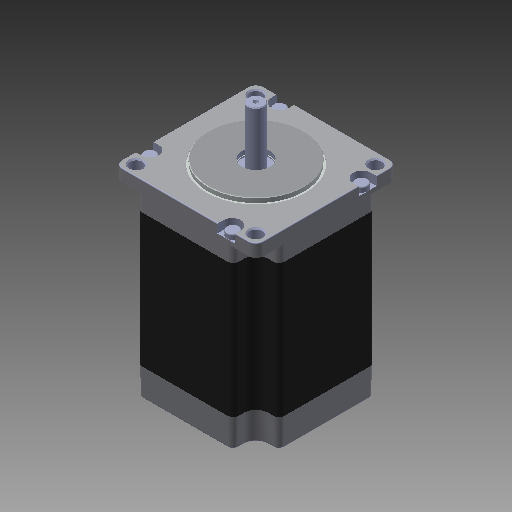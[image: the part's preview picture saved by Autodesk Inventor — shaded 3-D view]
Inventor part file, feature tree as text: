
AUTODESK INVENTOR PART (.ipt)
format: ipt  version: 2018 (Build 220112000, 112)  size: 415,744 bytes
history: native  units: in
note: dims shown in document units (in); Inventor stores cm internally (conversion verified against a paired STEP export)
features: other x3, imported_body x2, extrude x1, sketch x1
ambient origin geometry x8: Origin, YZ Plane, XZ Plane, XY Plane, X Axis, Y Axis, Z Axis, Center Point
bodies: Body1 (feature_tree), Body2 (feature_tree), Body3 (feature_tree), Body4 (feature_tree)
feature tree (7):
  other  "Фаска2"
  other  "stepper motor NEMA 23 57x761"
  extrude  "Extrusion1"  [1 undecoded]
  other  "Вырез-Вытянуть12"
  imported_body  "Base1"
  imported_body  "Base2"
  sketch  "Sketch1"  dims[d0=0.5906in d1=0.0in]
note: 1 required parameter value undecoded (feature->parameter linkage not recoverable at this tier; creation-order binding heuristic only, values carry confidence <= 0.55)
